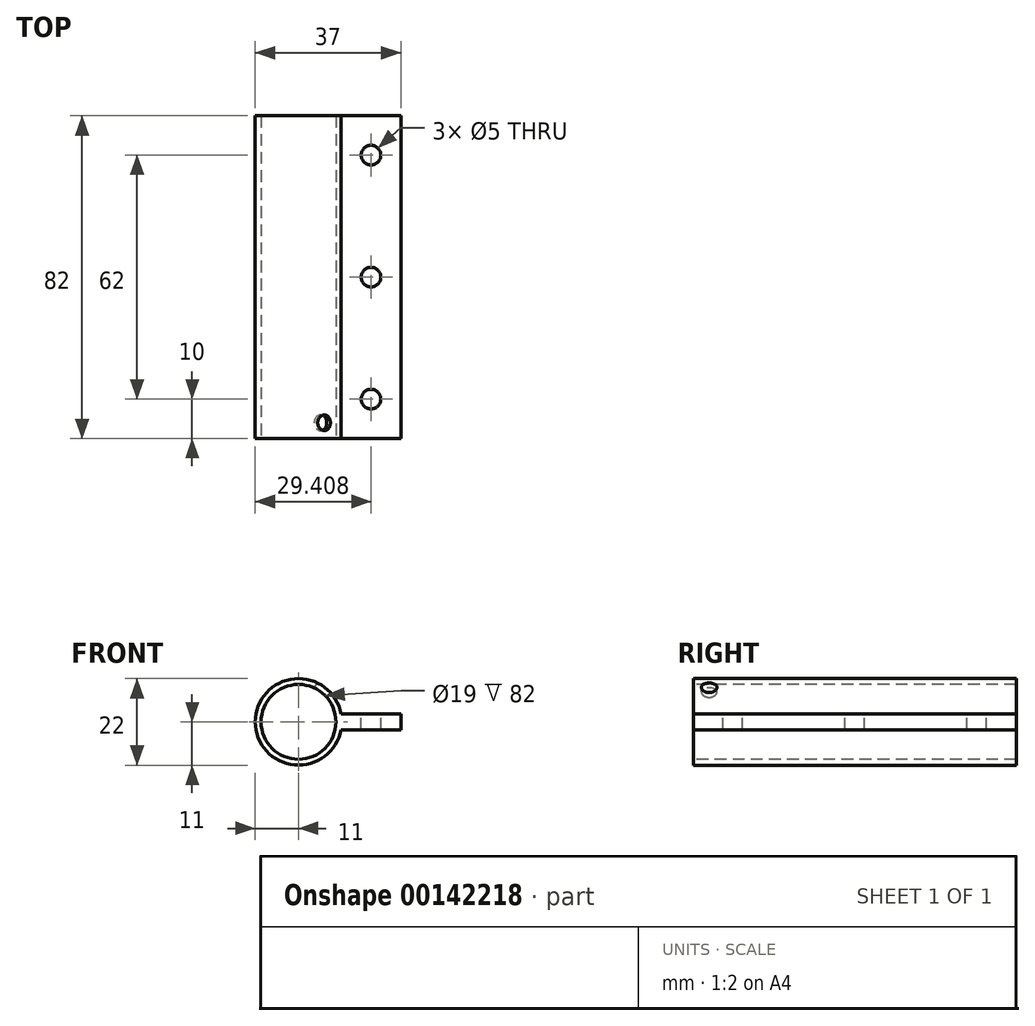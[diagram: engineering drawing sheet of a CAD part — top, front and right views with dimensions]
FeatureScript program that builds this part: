
annotation { "Feature Type Name" : "Feature", "Feature Type Description" : "" }
export const myFeature = defineFeature(function(context is Context, id is Id, definition is map)
    precondition{}
    {
        {
            var Q0;
            Q0=qCreatedBy(makeId("Front.planeOp"),FACE);
            var sketch = newSketch(context, id + "F0", { "sketchPlane" : qUnion([Q0])});
            skCircle(sketch, "E0", {"center": v(0, 0) * mm, "radius": 9.5 * mm});
            skCircle(sketch, "E1", {"center": v(0, 0) * mm, "radius": 11 * mm});
            skLineSegment(sketch, "E2", {"start": v(0, 0) * mm, "end": v(30, 0) * mm, "construction": true});
            skPoint(sketch, "E3", {"position": v(26, 0) * mm});
            skLineSegment(sketch, "E4", {"start": v(26, 2) * mm, "end": v(26, -2) * mm});
            skLineSegment(sketch, "E5", {"start": v(26, 2) * mm, "end": v(10.82, 2) * mm});
            skLineSegment(sketch, "E6", {"start": v(26, -2) * mm, "end": v(10.82, -2) * mm});
            skSolve(sketch);
        }
        {
            var Q0;
            Q0=qSketchRegion(id+"F0",true);
            extrude(context, id + "F1", {"entities" : qUnion([Q0]), "oppositeDirection" : true, "depth" : 82 * mm});
        }
        {
            var Q0;
            Q0=makeQuery(id+"F1.opExtrude","SWEPT_FACE",FACE,{"disambiguationData":[OSD([sQuery(id+"F0.wireOp",EDGE,"E5")])]});
            var sketch = newSketch(context, id + "F2", { "sketchPlane" : qUnion([Q0])});
            skLineSegment(sketch, "E7.0", {"start": v(26, 82) * mm, "end": v(10.82, 82) * mm, "construction": true});
            skLineSegment(sketch, "E8.0", {"start": v(26, 0) * mm, "end": v(10.82, 0) * mm, "construction": true});
            skPoint(sketch, "E9", {"position": v(18.4, 82) * mm});
            skPoint(sketch, "E10", {"position": v(18.4, 0) * mm});
            skPoint(sketch, "E11", {"position": v(18.4, 41) * mm});
            skCircle(sketch, "E12", {"center": v(18.4, 41) * mm, "radius": 2.5 * mm});
            skPoint(sketch, "E13", {"position": v(18.4, 72) * mm});
            skPoint(sketch, "E14", {"position": v(18.4, 10) * mm});
            skCircle(sketch, "E15", {"center": v(18.4, 72) * mm, "radius": 2.5 * mm});
            skCircle(sketch, "E16", {"center": v(18.4, 10) * mm, "radius": 2.5 * mm});
            skSolve(sketch);
        }
        {
            var Q0;
            Q0=makeQuery(id+"F2.imprint","IMPRINT",FACE,{"disambiguationData":[TD([[makeQuery(id+"F2.imprint","IMPRINT",EDGE,{"derivedFrom":sQuery(id+"F2.wireOp",EDGE,"E15")}),1.0]])]});
            var Q1;
            Q1=makeQuery(id+"F2.imprint","IMPRINT",FACE,{"disambiguationData":[TD([[makeQuery(id+"F2.imprint","IMPRINT",EDGE,{"derivedFrom":sQuery(id+"F2.wireOp",EDGE,"E12")}),1.0]])]});
            var Q2;
            Q2=makeQuery(id+"F2.imprint","IMPRINT",FACE,{"disambiguationData":[TD([[makeQuery(id+"F2.imprint","IMPRINT",EDGE,{"derivedFrom":sQuery(id+"F2.wireOp",EDGE,"E16")}),1.0]])]});
            extrude(context, id + "F3", {"entities" : qUnion([Q0, Q1, Q2]), "operationType" : NewBodyOperationType.REMOVE, "oppositeDirection" : true, "depth" : 25 * mm});
        }
        {
            var Q0;
            Q0=makeQuery(id+"F1.opExtrude","CAP_FACE",FACE,{"disambiguationData":[OSD([sQuery(id+"F0.wireOp",EDGE,"E0"),sQuery(id+"F0.wireOp",EDGE,"E1"),sQuery(id+"F0.wireOp",EDGE,"E4"),sQuery(id+"F0.wireOp",EDGE,"E5"),sQuery(id+"F0.wireOp",EDGE,"E6")])],"isStart":true});
            var sketch = newSketch(context, id + "F4", { "sketchPlane" : qUnion([Q0])});
            skLineSegment(sketch, "E17.0", {"start": v(26, 2) * mm, "end": v(10.82, 2) * mm, "construction": true});
            skArc(sketch, "E18.0", {"start": v(10.82, 2) * mm, "mid": v(-11, 0) * mm, "end": v(10.82, -2) * mm, "construction": true});
            skCircle(sketch, "E19.0", {"center": v(0, 0) * mm, "radius": 9.5 * mm, "construction": true});
            skLineSegment(sketch, "E20", {"start": v(10.82, 2) * mm, "end": v(6.6, 8.8) * mm, "construction": true});
            skLineSegment(sketch, "E21", {"start": v(5.83, 9.38) * mm, "end": v(7.53, 8.1) * mm, "construction": true});
            skSolve(sketch);
        }
        {
            var Q0;
            Q0=sQuery(id+"F4.wireOp",EDGE,"E21");
            cPlane(context, id + "F5", {"entities" : qUnion([Q0]), "cplaneType" : CPlaneType.LINE_ANGLE, "offset" : 25 * mm, "angle" : 90 * degree, "width" : 150 * mm, "height" : 150 * mm});
        }
        {
            var Q0;
            Q0=qCreatedBy(id+"F5.planeOp",FACE);
            var sketch = newSketch(context, id + "F6", { "sketchPlane" : qUnion([Q0])});
            skLineSegment(sketch, "E22", {"start": v(0, 0) * mm, "end": v(0, 4) * mm, "construction": true});
            skCircle(sketch, "E23", {"center": v(0, 4) * mm, "radius": 2 * mm});
            skSolve(sketch);
        }
        {
            var Q0;
            Q0=qSketchRegion(id+"F6",true);
            extrude(context, id + "F7", {"entities" : qUnion([Q0]), "operationType" : NewBodyOperationType.REMOVE, "oppositeDirection" : true, "depth" : 5 * mm});
        }
    });
